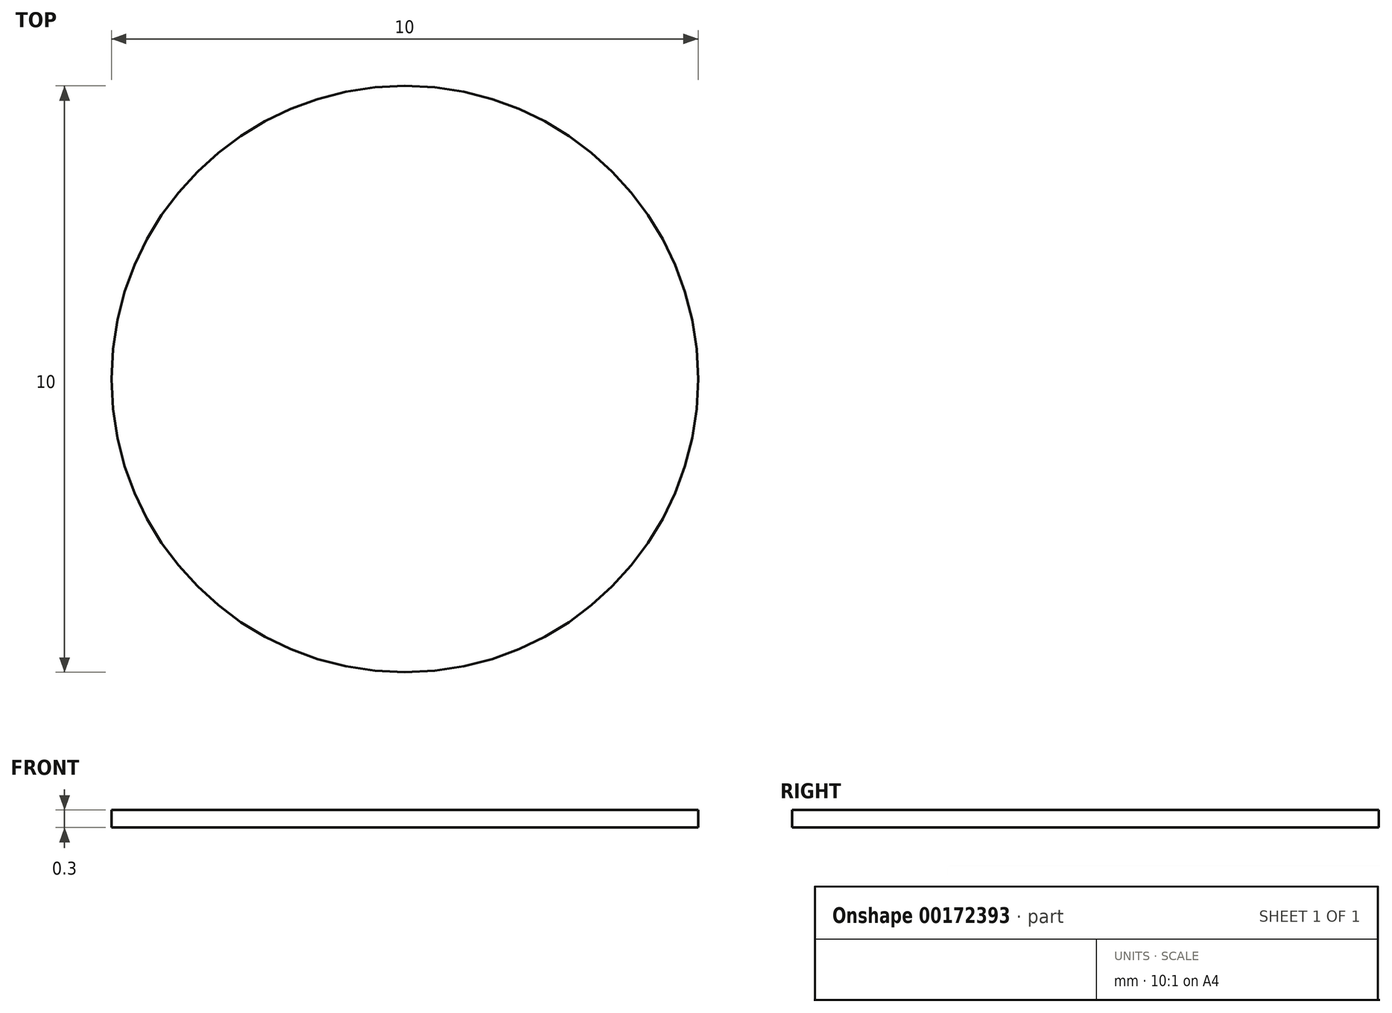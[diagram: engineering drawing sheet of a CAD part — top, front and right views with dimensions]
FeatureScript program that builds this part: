
annotation { "Feature Type Name" : "Feature", "Feature Type Description" : "" }
export const myFeature = defineFeature(function(context is Context, id is Id, definition is map)
    precondition{}
    {
        {
            var Q0;
            Q0=qCreatedBy(makeId("Top.planeOp"),FACE);
            var sketch = newSketch(context, id + "F0", { "sketchPlane" : qUnion([Q0])});
            skCircle(sketch, "E0", {"center": v(0, 0) * mm, "radius": 5 * mm});
            skSolve(sketch);
        }
        {
            var Q0;
            Q0=makeQuery(id+"F0.imprint","IMPRINT",FACE,{"disambiguationData":[TD([[makeQuery(id+"F0.imprint","IMPRINT",EDGE,{"derivedFrom":sQuery(id+"F0.wireOp",EDGE,"E0")}),1.0]])]});
            extrude(context, id + "F1", {"entities" : qUnion([Q0]), "depth" : 0.3 * mm});
        }
    });
